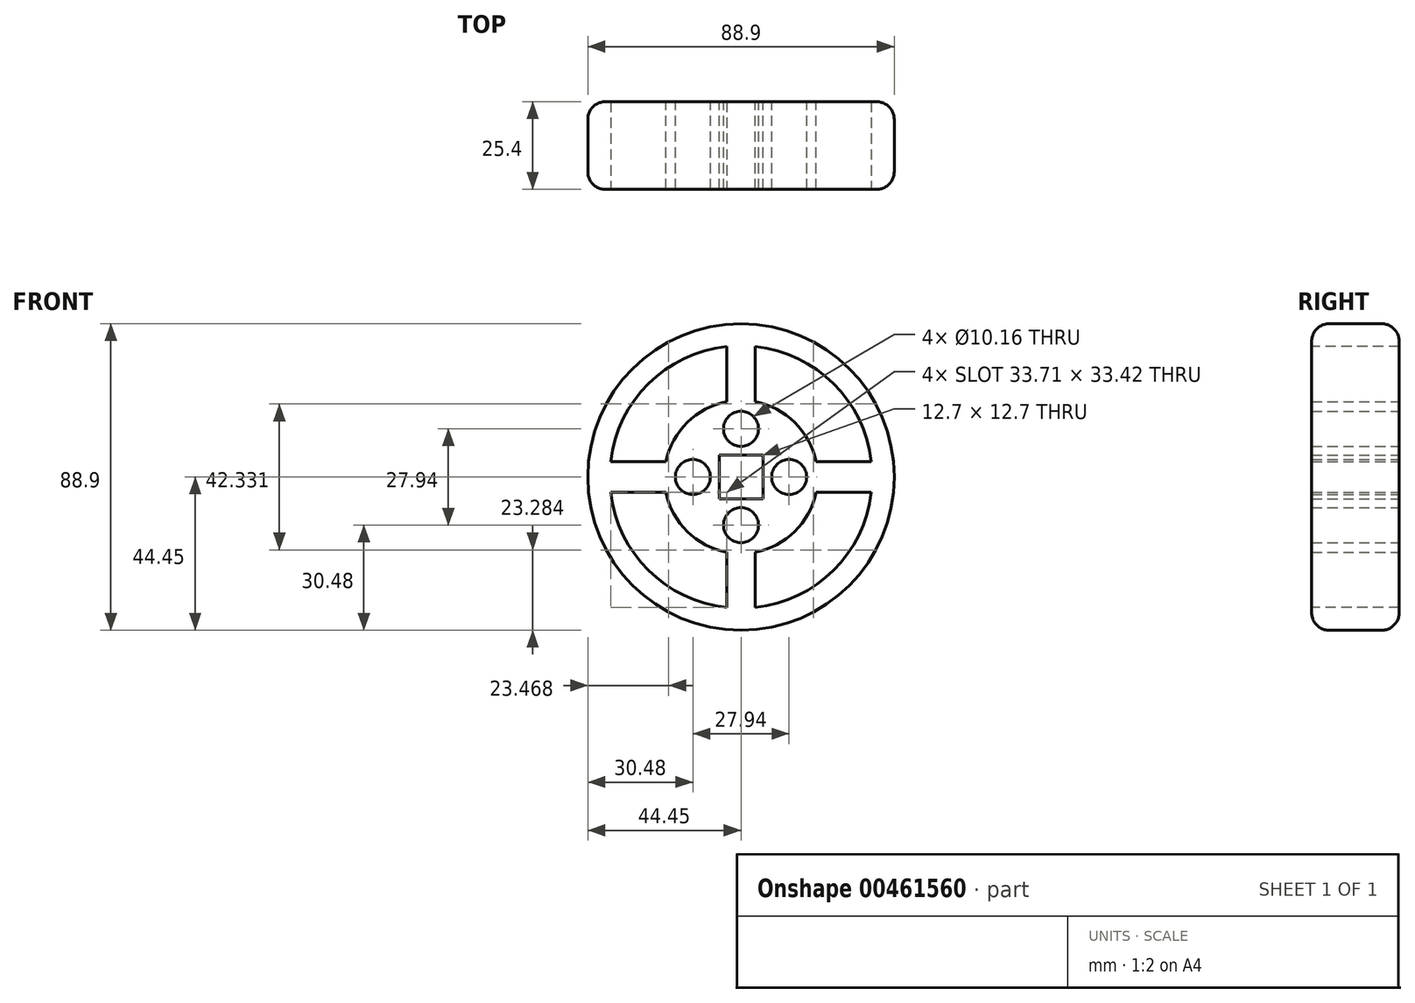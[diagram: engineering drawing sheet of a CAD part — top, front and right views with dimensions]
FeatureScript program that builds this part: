
annotation { "Feature Type Name" : "Feature", "Feature Type Description" : "" }
export const myFeature = defineFeature(function(context is Context, id is Id, definition is map)
    precondition{}
    {
        {
            var Q0;
            Q0=qCreatedBy(makeId("Front.planeOp"),FACE);
            var sketch = newSketch(context, id + "F0", { "sketchPlane" : qUnion([Q0])});
            skCircle(sketch, "E0", {"center": v(0, 0) * mm, "radius": 44.45 * mm});
            skSolve(sketch);
        }
        {
            var Q0;
            Q0=makeQuery(id+"F0.imprint","IMPRINT",FACE,{"disambiguationData":[TD([[makeQuery(id+"F0.imprint","IMPRINT",EDGE,{"derivedFrom":sQuery(id+"F0.wireOp",EDGE,"E0")}),1.0]])]});
            extrude(context, id + "F1", {"entities" : qUnion([Q0]), "depth" : 12.7 * mm});
        }
        {
            var Q0;
            Q0=makeQuery(id+"F1.opExtrude","CAP_FACE",FACE,{"disambiguationData":[OSD([sQuery(id+"F0.wireOp",EDGE,"E0")])],"isStart":false});
            var sketch = newSketch(context, id + "F2", { "sketchPlane" : qUnion([Q0])});
            skCircle(sketch, "E1", {"center": v(0, 0) * mm, "radius": 50.8 * mm});
            skSolve(sketch);
        }
        {
            var Q0;
            Q0=sQuery(id+"F2.wireOp",VERTEX,"E1.center");
            var Q1;
            Q1=makeQuery(id+"F1.opExtrude","SWEPT_BODY",BODY,{"disambiguationData":[OSD([sQuery(id+"F0.wireOp",EDGE,"E0")])]});
            hole(context, id + "F3", {"style" : HoleStyle.SIMPLE, "endStyle" : HoleEndStyle.THROUGH, "holeDiameter" : 76.2 * mm, "isTappedThrough" : true, "tappedDepth" : 12.7 * mm, "tapClearance" : 3, "locations" : qUnion([Q0]), "scope" : qUnion([Q1])});
        }
        {
            var Q0;
            Q0=qCreatedBy(makeId("Front.planeOp"),FACE);
            var sketch = newSketch(context, id + "F4", { "sketchPlane" : qUnion([Q0])});
            skLineSegment(sketch, "E2.bottom", {"start": v(4.13, -42.15) * mm, "end": v(-4.13, -42.15) * mm});
            skLineSegment(sketch, "E2.top", {"start": v(4.13, 42.15) * mm, "end": v(-4.13, 42.15) * mm});
            skLineSegment(sketch, "E2.left", {"start": v(4.13, -42.15) * mm, "end": v(4.13, 42.15) * mm});
            skLineSegment(sketch, "E2.right", {"start": v(-4.13, -42.15) * mm, "end": v(-4.13, 42.15) * mm});
            skPoint(sketch, "E2.middle", {"position": v(0, 0) * mm});
            skLineSegment(sketch, "E3.bottom", {"start": v(42.66, 4.46) * mm, "end": v(-42.66, 4.46) * mm});
            skLineSegment(sketch, "E3.top", {"start": v(42.66, -4.46) * mm, "end": v(-42.66, -4.46) * mm});
            skLineSegment(sketch, "E3.left", {"start": v(42.66, 4.46) * mm, "end": v(42.66, -4.46) * mm});
            skLineSegment(sketch, "E3.right", {"start": v(-42.66, 4.46) * mm, "end": v(-42.66, -4.46) * mm});
            skSolve(sketch);
        }
        {
            var Q0;
            {var subQ5=sQuery(id+"F4.wireOp",EDGE,"E3.left");Q0=makeQuery(id+"F4.imprint","IMPRINT",FACE,{"disambiguationData":[TD([[makeQuery(id+"F4.imprint","IMPRINT",EDGE,{"derivedFrom":subQ5}),-1.0]])]});}
            var Q1;
            {var subQ5=sQuery(id+"F4.wireOp",EDGE,"E3.right");Q1=makeQuery(id+"F4.imprint","IMPRINT",FACE,{"disambiguationData":[TD([[makeQuery(id+"F4.imprint","IMPRINT",EDGE,{"derivedFrom":subQ5}),1.0]])]});}
            var Q2;
            {var subQ0=sQuery(id+"F4.wireOp",EDGE,"E3.top");var subQ1=sQuery(id+"F4.wireOp",EDGE,"E2.left");var subQ2=makeQuery(id+"F4.imprint","INTERSECT",VERTEX,{"derivedFrom":[subQ1,subQ0]});Q2=makeQuery(id+"F4.imprint","IMPRINT",FACE,{"disambiguationData":[TD([[makeQuery(id+"F4.imprint","IMPRINT",EDGE,{"disambiguationData":[TD([[subQ2,-1.0]])],"derivedFrom":subQ1}),1.0]])]});}
            var Q3;
            {var subQ0=sQuery(id+"F4.wireOp",EDGE,"E2.top");Q3=makeQuery(id+"F4.imprint","IMPRINT",FACE,{"disambiguationData":[TD([[makeQuery(id+"F4.imprint","IMPRINT",EDGE,{"derivedFrom":subQ0}),1.0]])]});}
            var Q4;
            {var subQ0=sQuery(id+"F4.wireOp",EDGE,"E2.bottom");Q4=makeQuery(id+"F4.imprint","IMPRINT",FACE,{"disambiguationData":[TD([[makeQuery(id+"F4.imprint","IMPRINT",EDGE,{"derivedFrom":subQ0}),-1.0]])]});}
            extrude(context, id + "F5", {"entities" : qUnion([Q0, Q1, Q2, Q3, Q4]), "operationType" : NewBodyOperationType.ADD, "depth" : 12.7 * mm});
        }
        {
            var Q0;
            Q0=qCreatedBy(makeId("Front.planeOp"),FACE);
            var sketch = newSketch(context, id + "F6", { "sketchPlane" : qUnion([Q0])});
            skCircle(sketch, "E4", {"center": v(0, 0) * mm, "radius": 22.23 * mm});
            skSolve(sketch);
        }
        {
            var Q0;
            Q0=makeQuery(id+"F6.imprint","IMPRINT",FACE,{"disambiguationData":[TD([[makeQuery(id+"F6.imprint","IMPRINT",EDGE,{"derivedFrom":sQuery(id+"F6.wireOp",EDGE,"E4")}),1.0]])]});
            extrude(context, id + "F7", {"entities" : qUnion([Q0]), "operationType" : NewBodyOperationType.ADD, "depth" : 12.7 * mm});
        }
        {
            var Q0;
            Q0=qCreatedBy(makeId("Front.planeOp"),FACE);
            var sketch = newSketch(context, id + "F8", { "sketchPlane" : qUnion([Q0])});
            skCircle(sketch, "E5", {"center": v(0, 13.97) * mm, "radius": 5.08 * mm});
            skCircle(sketch, "E6", {"center": v(13.97, 0) * mm, "radius": 5.08 * mm});
            skCircle(sketch, "E7", {"center": v(0, -13.97) * mm, "radius": 5.08 * mm});
            skCircle(sketch, "E8", {"center": v(-13.97, 0) * mm, "radius": 5.08 * mm});
            skSolve(sketch);
        }
        {
            var Q0;
            Q0 = qSketchRegion(id + "F8", true);
            extrude(context, id + "F9", {"entities" : qUnion([Q0]), "operationType" : NewBodyOperationType.REMOVE, "endBound" : BoundingType.THROUGH_ALL, "depth" : 25.4 * mm});
        }
        {
            var Q0;
            Q0=makeQuery(id+"F1.opExtrude","SWEPT_BODY",BODY,{"disambiguationData":[OSD([sQuery(id+"F0.wireOp",EDGE,"E0")])]});
            var Q1;
            Q1=qCreatedBy(makeId("Front.planeOp"),FACE);
            mirror(context, id + "F10", {"operationType" : NewBodyOperationType.ADD, "entities" : qUnion([Q0]), "mirrorPlane" : qUnion([Q1])});
        }
        {
            var Q0;
            {var subQ0=makeQuery(id+"F1.opExtrude","SWEPT_FACE",FACE,{"disambiguationData":[OSD([sQuery(id+"F0.wireOp",EDGE,"E0")])]});Q0=makeQuery(id+"F10.boolean.opBoolean","MERGE",FACE,{"derivedFrom":[subQ0,makeQuery(id+"F10.opPattern","COPY",FACE,{"derivedFrom":subQ0,"instanceName":"1"})]});}
            fillet(context, id + "F11", {"entities" : qUnion([Q0]), "radius" : 5.08 * mm, "tangentPropagation" : true, "allowEdgeOverflow" : false});
        }
        {
            var Q0;
            Q0=makeQuery(id+"F10.opPattern","COPY",FACE,{"derivedFrom":makeQuery(id+"F7.boolean.opBoolean","MERGE",FACE,{"derivedFrom":[makeQuery(id+"F5.boolean.opBoolean","MERGE",FACE,{"derivedFrom":[makeQuery(id+"F1.opExtrude","CAP_FACE",FACE,{"disambiguationData":[OSD([sQuery(id+"F0.wireOp",EDGE,"E0")])],"isStart":false}),makeQuery(id+"F5.opExtrude","CAP_FACE",FACE,{"disambiguationData":[OSD([sQuery(id+"F4.wireOp",EDGE,"E2.bottom"),sQuery(id+"F4.wireOp",EDGE,"E2.top"),sQuery(id+"F4.wireOp",EDGE,"E2.left"),sQuery(id+"F4.wireOp",EDGE,"E2.right"),sQuery(id+"F4.wireOp",EDGE,"E3.bottom"),sQuery(id+"F4.wireOp",EDGE,"E3.top"),sQuery(id+"F4.wireOp",EDGE,"E3.left"),sQuery(id+"F4.wireOp",EDGE,"E3.right")])],"isStart":false})]}),makeQuery(id+"F7.opExtrude","CAP_FACE",FACE,{"disambiguationData":[OSD([sQuery(id+"F6.wireOp",EDGE,"E4")])],"isStart":false})]}),"instanceName":"1"});
            var sketch = newSketch(context, id + "F12", { "sketchPlane" : qUnion([Q0])});
            skLineSegment(sketch, "E9.bottom", {"start": v(6.35, -6.35) * mm, "end": v(-6.35, -6.35) * mm});
            skLineSegment(sketch, "E9.top", {"start": v(6.35, 6.35) * mm, "end": v(-6.35, 6.35) * mm});
            skLineSegment(sketch, "E9.left", {"start": v(6.35, -6.35) * mm, "end": v(6.35, 6.35) * mm});
            skLineSegment(sketch, "E9.right", {"start": v(-6.35, -6.35) * mm, "end": v(-6.35, 6.35) * mm});
            skPoint(sketch, "E9.middle", {"position": v(0, 0) * mm});
            skSolve(sketch);
        }
        {
            var Q0;
            Q0=makeQuery(id+"F12.imprint","IMPRINT",FACE,{"disambiguationData":[TD([[makeQuery(id+"F12.imprint","IMPRINT",EDGE,{"derivedFrom":sQuery(id+"F12.wireOp",EDGE,"E9.bottom")}),-1.0]])]});
            extrude(context, id + "F13", {"entities" : qUnion([Q0]), "operationType" : NewBodyOperationType.REMOVE, "endBound" : BoundingType.THROUGH_ALL, "oppositeDirection" : true, "depth" : 25.4 * mm});
        }
    });
